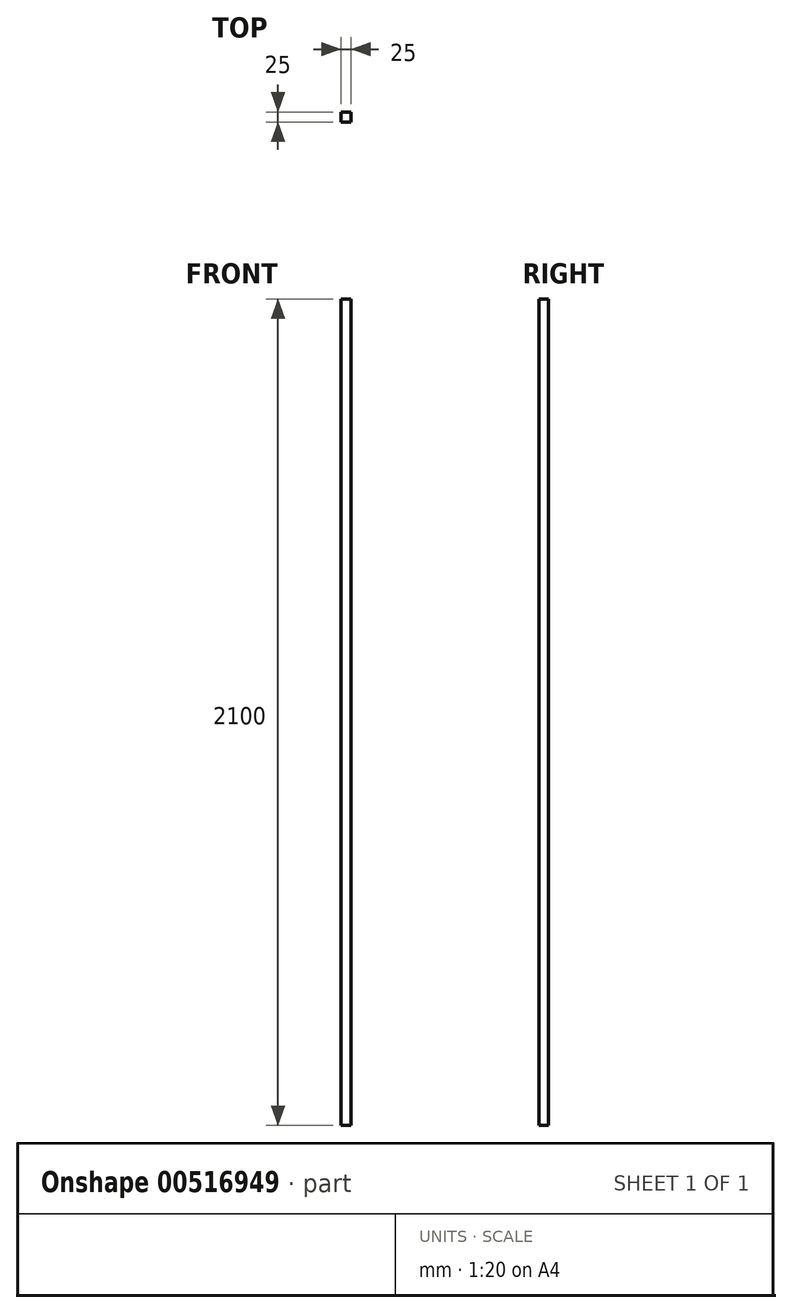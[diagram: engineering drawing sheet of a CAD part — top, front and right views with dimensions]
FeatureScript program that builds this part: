
annotation { "Feature Type Name" : "Feature", "Feature Type Description" : "" }
export const myFeature = defineFeature(function(context is Context, id is Id, definition is map)
    precondition{}
    {
        {
            var Q0;
            Q0=qCreatedBy(makeId("Top.planeOp"),FACE);
            var sketch = newSketch(context, id + "F0", { "sketchPlane" : qUnion([Q0])});
            skLineSegment(sketch, "E0.bottom", {"start": v(-46.16, 55.04) * mm, "end": v(-21.16, 55.04) * mm});
            skLineSegment(sketch, "E0.top", {"start": v(-46.16, 30.04) * mm, "end": v(-21.16, 30.04) * mm});
            skLineSegment(sketch, "E0.left", {"start": v(-46.16, 55.04) * mm, "end": v(-46.16, 30.04) * mm});
            skLineSegment(sketch, "E0.right", {"start": v(-21.16, 55.04) * mm, "end": v(-21.16, 30.04) * mm});
            skSolve(sketch);
        }
        {
            var Q0;
            Q0=makeQuery(id+"F0.imprint","IMPRINT",FACE,{"disambiguationData":[TD([[makeQuery(id+"F0.imprint","IMPRINT",EDGE,{"derivedFrom":sQuery(id+"F0.wireOp",EDGE,"E0.bottom")}),-1.0]])]});
            extrude(context, id + "F1", {"entities" : qUnion([Q0]), "depth" : 2100 * mm, "offsetDistance" : 25 * mm});
        }
    });
